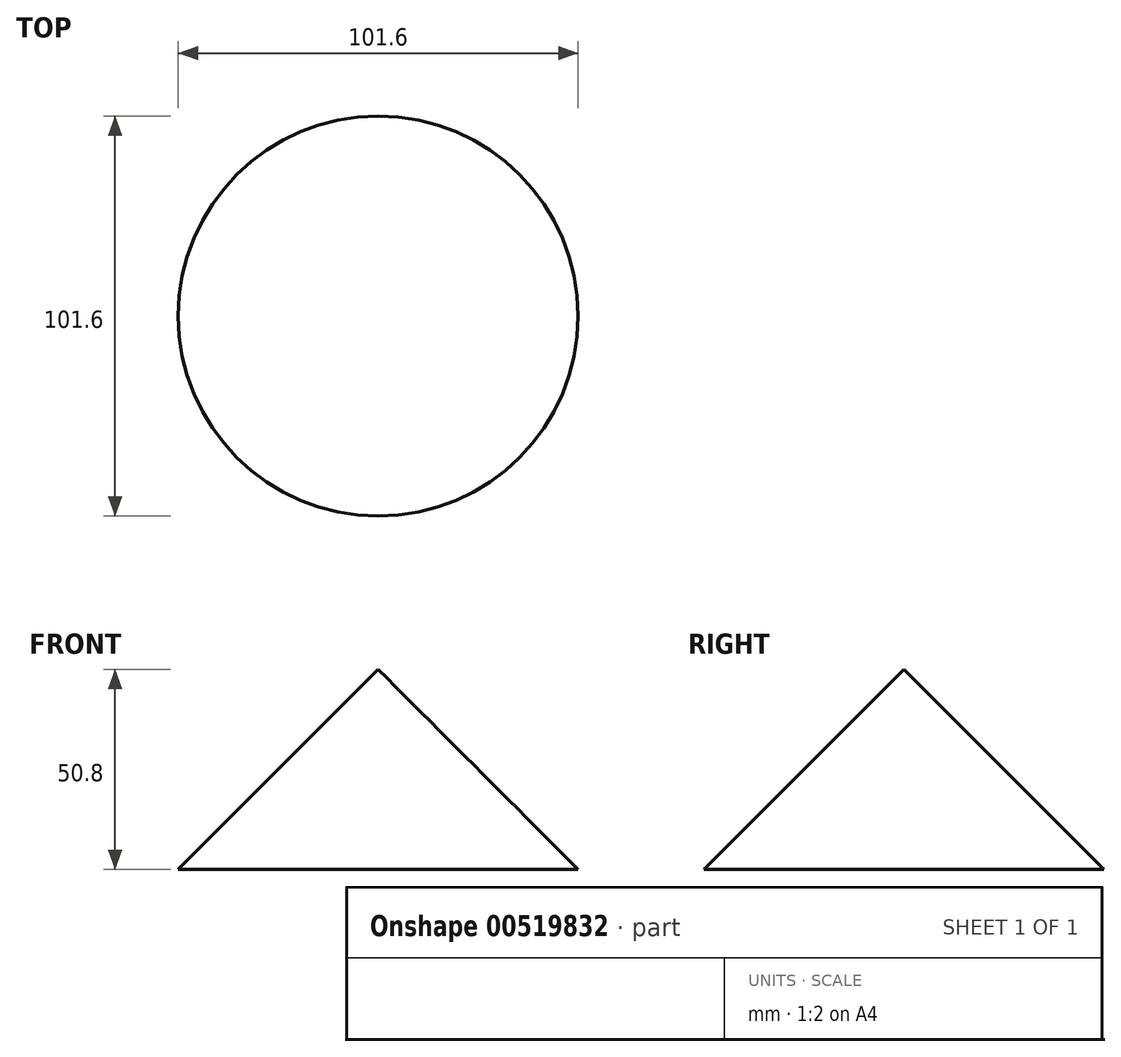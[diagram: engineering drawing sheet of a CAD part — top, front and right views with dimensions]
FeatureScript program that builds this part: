
annotation { "Feature Type Name" : "Feature", "Feature Type Description" : "" }
export const myFeature = defineFeature(function(context is Context, id is Id, definition is map)
    precondition{}
    {
        {
            var Q0;
            Q0=qCreatedBy(makeId("Top.planeOp"),FACE);
            var sketch = newSketch(context, id + "F0", { "sketchPlane" : qUnion([Q0])});
            skPoint(sketch, "E0.middle", {"position": v(0, 0) * mm});
            skCircle(sketch, "E1", {"center": v(0, 0) * mm, "radius": 25.4 * mm});
            skSolve(sketch);
        }
        {
            var Q0;
            Q0=makeQuery(id+"F0.imprint","IMPRINT",FACE,{"disambiguationData":[TD([[makeQuery(id+"F0.imprint","IMPRINT",EDGE,{"derivedFrom":sQuery(id+"F0.wireOp",EDGE,"E0.bottom")}),1.0]])]});
            var Q1;
            Q1=makeQuery(id+"F0.imprint","IMPRINT",FACE,{"disambiguationData":[TD([[makeQuery(id+"F0.imprint","IMPRINT",EDGE,{"derivedFrom":sQuery(id+"F0.wireOp",EDGE,"E1")}),1.0]])]});
            extrude(context, id + "F1", {"entities" : qUnion([Q0, Q1]), "depth" : 25.4 * mm, "offsetDistance" : 25.4 * mm, "hasDraft" : true, "draftAngle" : 45 * degree, "draftPullDirection" : true, "hasSecondDirection" : true, "secondDirectionOppositeDirection" : true, "secondDirectionDepth" : 25.4 * mm, "hasSecondDirectionDraft" : true, "secondDirectionDraftAngle" : 45 * degree});
        }
    });
